# Revit family: Sanitary_Showers_hansgrohe_26843USA-Rainfinity-Wall-outlet-Porter-5_NEW
name_source: partatom
category: Plumbing Fixtures
revit_build: Autodesk Revit 2018 (Build: 20170223_1515(x64)
units: mm (PartAtom-declared; Revit-internal decimal feet)

## family parameters
Always vertical = No
Cut with Voids When Loaded = No
OmniClass Number = 23.31.17.00
OmniClass Title = Showers
Part Type = Normal
Room Calculation Point = No
Round Connector Dimension = Use Diameter
Shared = No
Work Plane-Based = Yes

## types (1)
- 701 Matt White
    Always visible = Yes
    BIMobject category = Showers
    Connector Description = Water Inlet 1/2
    Default Elevation = 4' - 0"
    Description = Rainfinity Wall outlet Porter 500 with shower holder left and shower shelf L
    Diameter = 1"
    Edition number = 1
    IFC Classification = Sanitary Terminal
    Manufacturer = Hansgrohe
    Manufacturer name = hansgrohe
    Material 1 = Hansgrohe - Plastic - Graphite
    Material 2 = Hansgrohe - Metal - 701 Matt White
    Model = 26843USA
    OmniClass Code = 23-31 17 00
    OmniClass Description = Showers
    Outlet Connector Description = Water Outlet 1/2
    Outlet Diameter = 1"
    Product Guid = 0aa42017-2b88-4ba2-b862-cbe2c7b3dff3
    Product SKU = 26843USA
    Product data url = https://bimobject.com
    Product family = Rainfinity
    Product group = Wall outlet
    Product name = 26843USA Rainfinity Wall outlet Porter 500 with shower holder left and shower shelf L
    Product url = https://www.hansgrohe.com
    QR code = https://bimobject.com
    URL = https://www.hansgrohe.com
    Weight Net (Kg) = 2

## geometry (parser evidence)
native form markers: Sweep x2
no freeform markers — native parametric forms only
